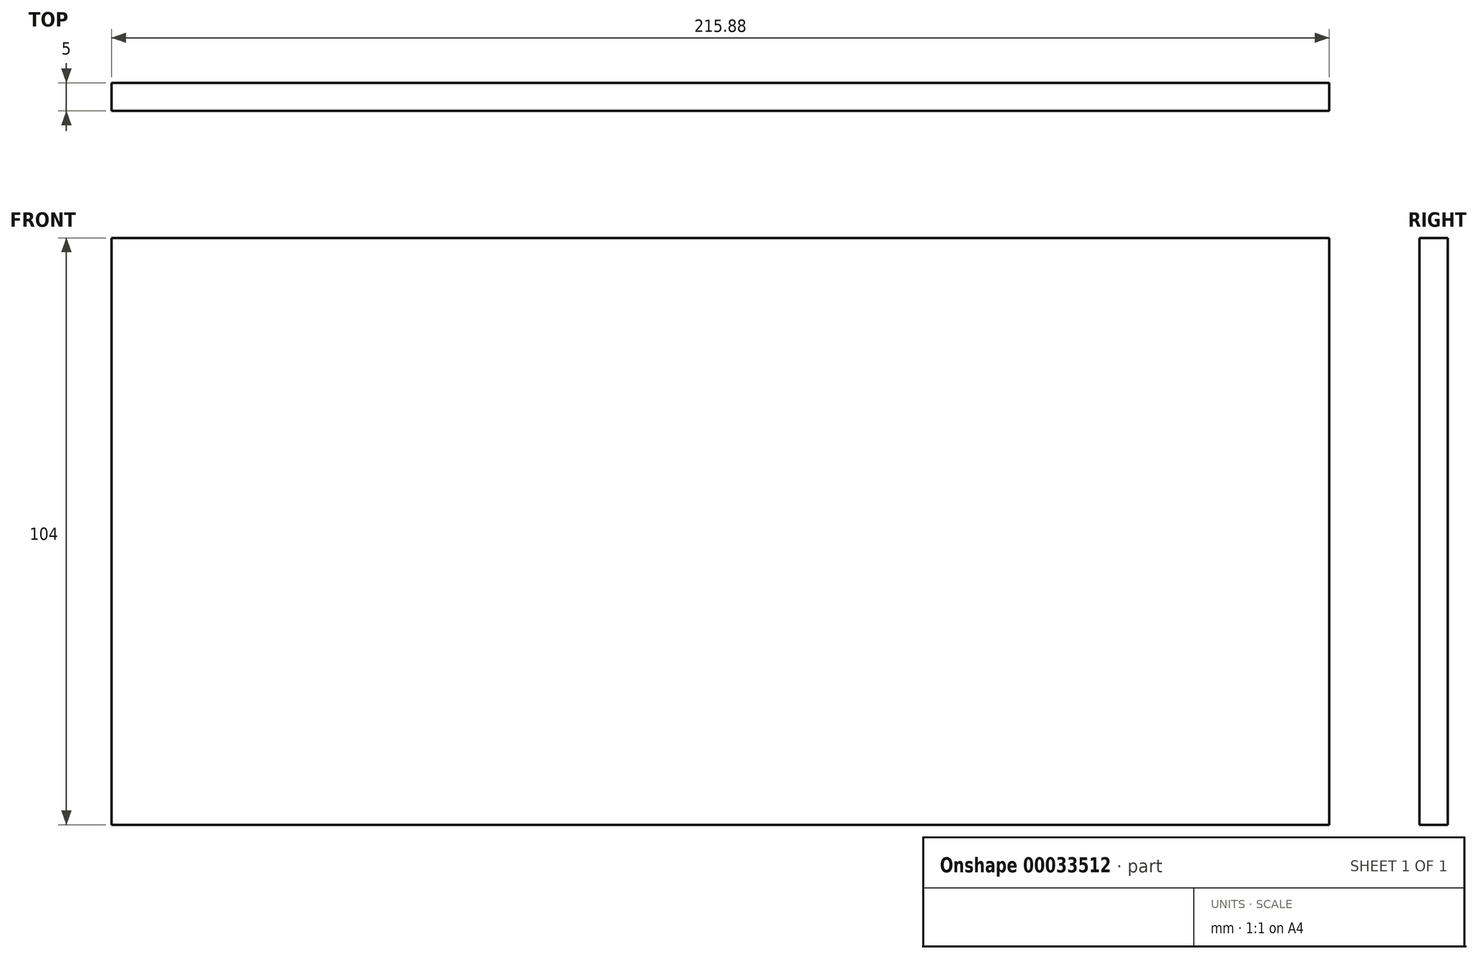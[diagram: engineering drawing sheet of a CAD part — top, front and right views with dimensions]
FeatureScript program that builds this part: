
annotation { "Feature Type Name" : "Feature", "Feature Type Description" : "" }
export const myFeature = defineFeature(function(context is Context, id is Id, definition is map)
    precondition{}
    {
        {
            var Q0;
            Q0=qCreatedBy(makeId("Front.planeOp"),FACE);
            var sketch = newSketch(context, id + "F0", { "sketchPlane" : qUnion([Q0])});
            skLineSegment(sketch, "E0.rect.bottom", {"start": v(107.94, 52) * mm, "end": v(-107.94, 52) * mm});
            skLineSegment(sketch, "E0.rect.top", {"start": v(107.94, -52) * mm, "end": v(-107.94, -52) * mm});
            skLineSegment(sketch, "E0.rect.left", {"start": v(107.94, 52) * mm, "end": v(107.94, -52) * mm});
            skLineSegment(sketch, "E0.rect.right", {"start": v(-107.94, 52) * mm, "end": v(-107.94, -52) * mm});
            skPoint(sketch, "E0.rect.middle", {"position": v(0, 0) * mm});
            skSolve(sketch);
        }
        {
            var Q0;
            Q0=makeQuery(id+"F0.imprint","IMPRINT",FACE,{"disambiguationData":[TD([[makeQuery(id+"F0.imprint","IMPRINT",EDGE,{"derivedFrom":sQuery(id+"F0.wireOp",EDGE,"E0.rect.bottom")}),1.0]])]});
            extrude(context, id + "F1", {"entities" : qUnion([Q0]), "depth" : 5 * mm});
        }
    });
